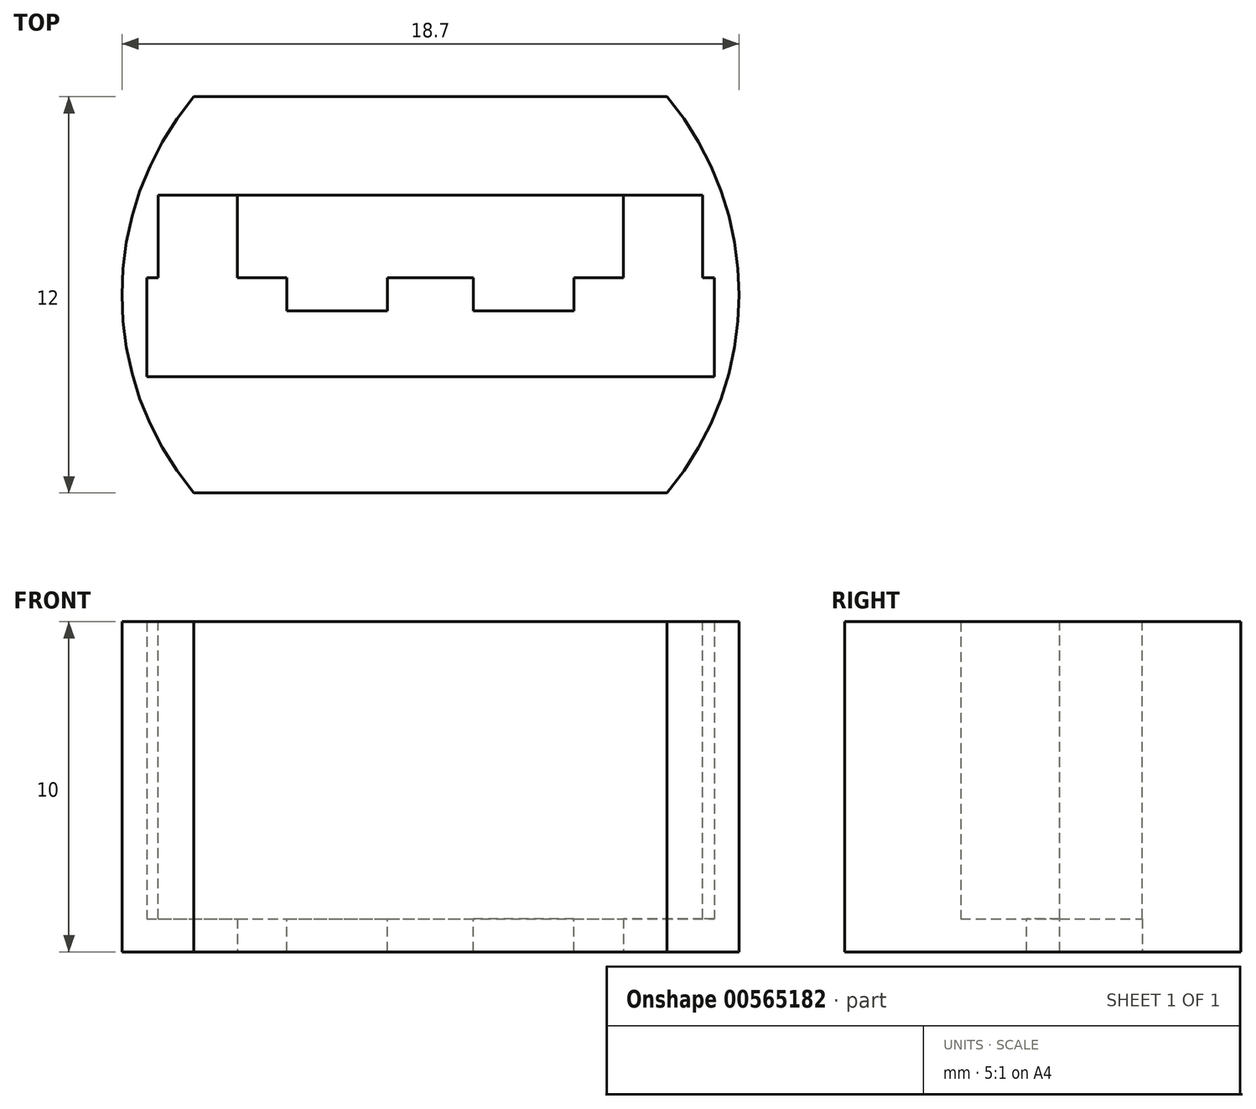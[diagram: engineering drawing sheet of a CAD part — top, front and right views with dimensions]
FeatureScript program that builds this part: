
annotation { "Feature Type Name" : "Feature", "Feature Type Description" : "" }
export const myFeature = defineFeature(function(context is Context, id is Id, definition is map)
    precondition{}
    {
        {
            var Q0;
            Q0=qCreatedBy(makeId("Top.planeOp"),FACE);
            var sketch = newSketch(context, id + "F0", { "sketchPlane" : qUnion([Q0])});
            skLineSegment(sketch, "E0.bottom", {"start": v(11, 6) * mm, "end": v(-11, 6) * mm});
            skLineSegment(sketch, "E0.top", {"start": v(11, -6) * mm, "end": v(-11, -6) * mm});
            skLineSegment(sketch, "E0.left", {"start": v(11, 6) * mm, "end": v(11, -6) * mm});
            skLineSegment(sketch, "E0.right", {"start": v(-11, 6) * mm, "end": v(-11, -6) * mm});
            skPoint(sketch, "E0.middle", {"position": v(0, 0) * mm});
            skLineSegment(sketch, "E1", {"start": v(0, 0) * mm, "end": v(0, -5.42) * mm, "construction": true});
            skLineSegment(sketch, "E2", {"start": v(0, -5.42) * mm, "end": v(0, 5.9) * mm, "construction": true});
            skLineSegment(sketch, "E3", {"start": v(0, 3.02) * mm, "end": v(5.85, 3.02) * mm});
            skLineSegment(sketch, "E4", {"start": v(5.85, 3.02) * mm, "end": v(5.85, 0.52) * mm});
            skLineSegment(sketch, "E5", {"start": v(5.85, 0.52) * mm, "end": v(8.6, 0.52) * mm});
            skLineSegment(sketch, "E6", {"start": v(8.6, 0.52) * mm, "end": v(8.6, -2.48) * mm});
            skLineSegment(sketch, "E7", {"start": v(8.6, -2.48) * mm, "end": v(0, -2.48) * mm});
            skLineSegment(sketch, "E8.MirrorCS", {"start": v(0, 3.02) * mm, "end": v(-5.85, 3.02) * mm});
            skLineSegment(sketch, "E9.MirrorCS", {"start": v(-5.85, 3.02) * mm, "end": v(-5.85, 0.52) * mm});
            skLineSegment(sketch, "E10.MirrorCS", {"start": v(-5.85, 0.52) * mm, "end": v(-8.6, 0.52) * mm});
            skLineSegment(sketch, "E11.MirrorCS", {"start": v(-8.6, 0.52) * mm, "end": v(-8.6, -2.48) * mm});
            skLineSegment(sketch, "E12.MirrorCS", {"start": v(-8.6, -2.48) * mm, "end": v(0, -2.48) * mm});
            skLineSegment(sketch, "E13", {"start": v(-5.85, 0.52) * mm, "end": v(5.85, 0.52) * mm});
            skSolve(sketch);
        }
        {
            var Q0;
            Q0=makeQuery(id+"F0.imprint","IMPRINT",FACE,{"disambiguationData":[TD([[makeQuery(id+"F0.imprint","IMPRINT",EDGE,{"derivedFrom":sQuery(id+"F0.wireOp",EDGE,"E0.bottom")}),1.0]])]});
            var Q1;
            Q1=makeQuery(id+"F0.imprint","IMPRINT",FACE,{"disambiguationData":[TD([[makeQuery(id+"F0.imprint","IMPRINT",EDGE,{"derivedFrom":sQuery(id+"F0.wireOp",EDGE,"E5")}),-1.0]])]});
            extrude(context, id + "F1", {"entities" : qUnion([Q0, Q1]), "depth" : 1 * mm, "offsetDistance" : 25 * mm});
        }
        {
            var Q0;
            Q0=qSketchRegion(id+"F0",true);
            extrude(context, id + "F2", {"entities" : qUnion([Q0]), "operationType" : NewBodyOperationType.ADD, "depth" : 10 * mm, "offsetDistance" : 25 * mm});
        }
        {
            var Q0;
            Q0=makeQuery(id+"F2.opExtrude","CAP_FACE",FACE,{"disambiguationData":[OSD([sQuery(id+"F0.wireOp",EDGE,"E0.bottom"),sQuery(id+"F0.wireOp",EDGE,"E0.top"),sQuery(id+"F0.wireOp",EDGE,"E0.left"),sQuery(id+"F0.wireOp",EDGE,"E0.right"),sQuery(id+"F0.wireOp",EDGE,"E3"),sQuery(id+"F0.wireOp",EDGE,"E4"),sQuery(id+"F0.wireOp",EDGE,"E5"),sQuery(id+"F0.wireOp",EDGE,"E6"),sQuery(id+"F0.wireOp",EDGE,"E7"),sQuery(id+"F0.wireOp",EDGE,"E8.MirrorCS"),sQuery(id+"F0.wireOp",EDGE,"E9.MirrorCS"),sQuery(id+"F0.wireOp",EDGE,"E10.MirrorCS"),sQuery(id+"F0.wireOp",EDGE,"E11.MirrorCS"),sQuery(id+"F0.wireOp",EDGE,"E12.MirrorCS")])],"isStart":false});
            var sketch = newSketch(context, id + "F3", { "sketchPlane" : qUnion([Q0])});
            skLineSegment(sketch, "E14.bottom", {"start": v(-5.85, 0.52) * mm, "end": v(-8.25, 0.52) * mm});
            skLineSegment(sketch, "E14.top", {"start": v(-5.85, 3.02) * mm, "end": v(-8.25, 3.02) * mm});
            skLineSegment(sketch, "E14.left", {"start": v(-5.85, 0.52) * mm, "end": v(-5.85, 3.02) * mm});
            skLineSegment(sketch, "E14.right", {"start": v(-8.25, 0.52) * mm, "end": v(-8.25, 3.02) * mm});
            skLineSegment(sketch, "E15.bottom", {"start": v(5.85, 0.52) * mm, "end": v(8.25, 0.52) * mm});
            skLineSegment(sketch, "E15.top", {"start": v(5.85, 3.02) * mm, "end": v(8.25, 3.02) * mm});
            skLineSegment(sketch, "E15.left", {"start": v(5.85, 0.52) * mm, "end": v(5.85, 3.02) * mm});
            skLineSegment(sketch, "E15.right", {"start": v(8.25, 0.52) * mm, "end": v(8.25, 3.02) * mm});
            skSolve(sketch);
        }
        {
            var Q0;
            Q0=makeQuery(id+"F3.imprint","IMPRINT",FACE,{"disambiguationData":[TD([[makeQuery(id+"F3.imprint","IMPRINT",EDGE,{"derivedFrom":sQuery(id+"F3.wireOp",EDGE,"E14.bottom")}),-1.0]])]});
            var Q1;
            Q1=makeQuery(id+"F3.imprint","IMPRINT",FACE,{"disambiguationData":[TD([[makeQuery(id+"F3.imprint","IMPRINT",EDGE,{"derivedFrom":sQuery(id+"F3.wireOp",EDGE,"E15.bottom")}),1.0]])]});
            var Q2;
            Q2=makeQuery(id+"F1.opExtrude","CAP_FACE",FACE,{"disambiguationData":[OSD([sQuery(id+"F0.wireOp",EDGE,"E0.bottom"),sQuery(id+"F0.wireOp",EDGE,"E0.top"),sQuery(id+"F0.wireOp",EDGE,"E0.left"),sQuery(id+"F0.wireOp",EDGE,"E0.right"),sQuery(id+"F0.wireOp",EDGE,"E3"),sQuery(id+"F0.wireOp",EDGE,"E4"),sQuery(id+"F0.wireOp",EDGE,"E8.MirrorCS"),sQuery(id+"F0.wireOp",EDGE,"E9.MirrorCS"),sQuery(id+"F0.wireOp",EDGE,"E13")])],"isStart":false});
            extrude(context, id + "F4", {"entities" : qUnion([Q0, Q1]), "operationType" : NewBodyOperationType.REMOVE, "endBound" : BoundingType.UP_TO_SURFACE, "oppositeDirection" : true, "depth" : 25 * mm, "endBoundEntityFace" : qUnion([Q2]), "offsetDistance" : 25 * mm});
        }
        {
            var Q0;
            {var subQ0=sQuery(id+"F0.wireOp",EDGE,"E0.right");var subQ1=sQuery(id+"F0.wireOp",EDGE,"E0.top");Q0=makeQuery(id+"F2.boolean.opBoolean","MERGE",EDGE,{"derivedFrom":[makeQuery(id+"F1.opExtrude","SWEPT_EDGE",EDGE,{"disambiguationData":[OSD([subQ1,subQ0])]}),makeQuery(id+"F2.opExtrude","SWEPT_EDGE",EDGE,{"disambiguationData":[OSD([subQ1,subQ0])]})]});}
            var Q1;
            {var subQ0=sQuery(id+"F0.wireOp",EDGE,"E0.left");var subQ1=sQuery(id+"F0.wireOp",EDGE,"E0.top");Q1=makeQuery(id+"F2.boolean.opBoolean","MERGE",EDGE,{"derivedFrom":[makeQuery(id+"F1.opExtrude","SWEPT_EDGE",EDGE,{"disambiguationData":[OSD([subQ1,subQ0])]}),makeQuery(id+"F2.opExtrude","SWEPT_EDGE",EDGE,{"disambiguationData":[OSD([subQ1,subQ0])]})]});}
            var Q2;
            {var subQ0=sQuery(id+"F0.wireOp",EDGE,"E0.right");var subQ1=sQuery(id+"F0.wireOp",EDGE,"E0.bottom");Q2=makeQuery(id+"F2.boolean.opBoolean","MERGE",EDGE,{"derivedFrom":[makeQuery(id+"F1.opExtrude","SWEPT_EDGE",EDGE,{"disambiguationData":[OSD([subQ1,subQ0])]}),makeQuery(id+"F2.opExtrude","SWEPT_EDGE",EDGE,{"disambiguationData":[OSD([subQ1,subQ0])]})]});}
            var Q3;
            {var subQ0=sQuery(id+"F0.wireOp",EDGE,"E0.left");var subQ1=sQuery(id+"F0.wireOp",EDGE,"E0.bottom");Q3=makeQuery(id+"F2.boolean.opBoolean","MERGE",EDGE,{"derivedFrom":[makeQuery(id+"F1.opExtrude","SWEPT_EDGE",EDGE,{"disambiguationData":[OSD([subQ1,subQ0])]}),makeQuery(id+"F2.opExtrude","SWEPT_EDGE",EDGE,{"disambiguationData":[OSD([subQ1,subQ0])]})]});}
            fillet(context, id + "F5", {"entities" : qUnion([Q0, Q1, Q2, Q3]), "radius" : 2 * mm, "tangentPropagation" : true, "allowEdgeOverflow" : false});
        }
        {
            var Q0;
            Q0=makeQuery(id+"F2.opExtrude","CAP_FACE",FACE,{"disambiguationData":[OSD([sQuery(id+"F0.wireOp",EDGE,"E0.bottom"),sQuery(id+"F0.wireOp",EDGE,"E0.top"),sQuery(id+"F0.wireOp",EDGE,"E0.left"),sQuery(id+"F0.wireOp",EDGE,"E0.right"),sQuery(id+"F0.wireOp",EDGE,"E3"),sQuery(id+"F0.wireOp",EDGE,"E4"),sQuery(id+"F0.wireOp",EDGE,"E5"),sQuery(id+"F0.wireOp",EDGE,"E6"),sQuery(id+"F0.wireOp",EDGE,"E7"),sQuery(id+"F0.wireOp",EDGE,"E8.MirrorCS"),sQuery(id+"F0.wireOp",EDGE,"E9.MirrorCS"),sQuery(id+"F0.wireOp",EDGE,"E10.MirrorCS"),sQuery(id+"F0.wireOp",EDGE,"E11.MirrorCS"),sQuery(id+"F0.wireOp",EDGE,"E12.MirrorCS")])],"isStart":false});
            var sketch = newSketch(context, id + "F6", { "sketchPlane" : qUnion([Q0])});
            skCircle(sketch, "E16", {"center": v(0, 0) * mm, "radius": 9.35 * mm});
            skCircle(sketch, "E17", {"center": v(0, 0) * mm, "radius": 12.5 * mm});
            skSolve(sketch);
        }
        {
            var Q0;
            Q0=makeQuery(id+"F6.imprint","IMPRINT",FACE,{"disambiguationData":[TD([[makeQuery(id+"F6.imprint","IMPRINT",EDGE,{"derivedFrom":sQuery(id+"F6.wireOp",EDGE,"E17")}),1.0]])]});
            var Q1;
            {var subQ0=sQuery(id+"F0.wireOp",EDGE,"E0.right");Q1=makeQuery(id+"F6.imprint","IMPRINT",FACE,{"disambiguationData":[TD([[makeQuery(id+"F6.imprint","IMPRINT",EDGE,{"derivedFrom":makeQuery(id+"F2.opExtrude","CAP_EDGE",EDGE,{"disambiguationData":[OSD([subQ0])],"isStart":false})}),1.0]])]});}
            var Q2;
            {var subQ0=sQuery(id+"F0.wireOp",EDGE,"E0.left");Q2=makeQuery(id+"F6.imprint","IMPRINT",FACE,{"disambiguationData":[TD([[makeQuery(id+"F6.imprint","IMPRINT",EDGE,{"derivedFrom":makeQuery(id+"F2.opExtrude","CAP_EDGE",EDGE,{"disambiguationData":[OSD([subQ0])],"isStart":false})}),-1.0]])]});}
            extrude(context, id + "F7", {"entities" : qUnion([Q0, Q1, Q2]), "operationType" : NewBodyOperationType.REMOVE, "oppositeDirection" : true, "depth" : 25 * mm, "offsetDistance" : 25 * mm});
        }
        {
            var Q0;
            {var subQ0=sQuery(id+"F0.wireOp",EDGE,"E13");var subQ1=sQuery(id+"F0.wireOp",EDGE,"E9.MirrorCS");var subQ2=sQuery(id+"F0.wireOp",EDGE,"E8.MirrorCS");var subQ3=sQuery(id+"F0.wireOp",EDGE,"E4");var subQ4=sQuery(id+"F0.wireOp",EDGE,"E3");var subQ5=sQuery(id+"F0.wireOp",EDGE,"E0.right");var subQ6=sQuery(id+"F0.wireOp",EDGE,"E0.left");var subQ7=sQuery(id+"F0.wireOp",EDGE,"E0.top");var subQ8=sQuery(id+"F0.wireOp",EDGE,"E0.bottom");Q0=makeQuery(id+"F4.boolean.opBoolean","MERGE",FACE,{"derivedFrom":[makeQuery(id+"F1.opExtrude","CAP_FACE",FACE,{"disambiguationData":[OSD([subQ8,subQ7,subQ6,subQ5,subQ4,subQ3,subQ2,subQ1,subQ0])],"isStart":false}),makeQuery(id+"F4.opExtrude","CAP_FACE",FACE,{"disambiguationData":[OSD([subQ8,subQ7,subQ6,subQ5,subQ4,subQ3,subQ2,subQ1,subQ0]),OD(0.0)],"isStart":false}),makeQuery(id+"F4.opExtrude","CAP_FACE",FACE,{"disambiguationData":[OSD([subQ8,subQ7,subQ6,subQ5,subQ4,subQ3,subQ2,subQ1,subQ0]),OD(1.0)],"isStart":false})]});}
            var sketch = newSketch(context, id + "F8", { "sketchPlane" : qUnion([Q0])});
            skLineSegment(sketch, "E18.bottom", {"start": v(-4.35, 0.52) * mm, "end": v(-1.3, 0.52) * mm});
            skLineSegment(sketch, "E18.top", {"start": v(-4.35, -0.48) * mm, "end": v(-1.3, -0.48) * mm});
            skLineSegment(sketch, "E18.left", {"start": v(-4.35, 0.52) * mm, "end": v(-4.35, -0.48) * mm});
            skLineSegment(sketch, "E18.right", {"start": v(-1.3, 0.52) * mm, "end": v(-1.3, -0.48) * mm});
            skLineSegment(sketch, "E19.bottom", {"start": v(4.35, 0.52) * mm, "end": v(1.3, 0.52) * mm});
            skLineSegment(sketch, "E19.top", {"start": v(4.35, -0.48) * mm, "end": v(1.3, -0.48) * mm});
            skLineSegment(sketch, "E19.left", {"start": v(4.35, 0.52) * mm, "end": v(4.35, -0.48) * mm});
            skLineSegment(sketch, "E19.right", {"start": v(1.3, 0.52) * mm, "end": v(1.3, -0.48) * mm});
            skSolve(sketch);
        }
        {
            var Q0;
            Q0=makeQuery(id+"F8.imprint","IMPRINT",FACE,{"disambiguationData":[TD([[makeQuery(id+"F8.imprint","IMPRINT",EDGE,{"derivedFrom":sQuery(id+"F8.wireOp",EDGE,"E18.bottom")}),-1.0]])]});
            var Q1;
            Q1=makeQuery(id+"F8.imprint","IMPRINT",FACE,{"disambiguationData":[TD([[makeQuery(id+"F8.imprint","IMPRINT",EDGE,{"derivedFrom":sQuery(id+"F8.wireOp",EDGE,"E19.bottom")}),-1.0]])]});
            extrude(context, id + "F9", {"entities" : qUnion([Q0, Q1]), "operationType" : NewBodyOperationType.REMOVE, "oppositeDirection" : true, "depth" : 25 * mm, "offsetDistance" : 25 * mm});
        }
    });
